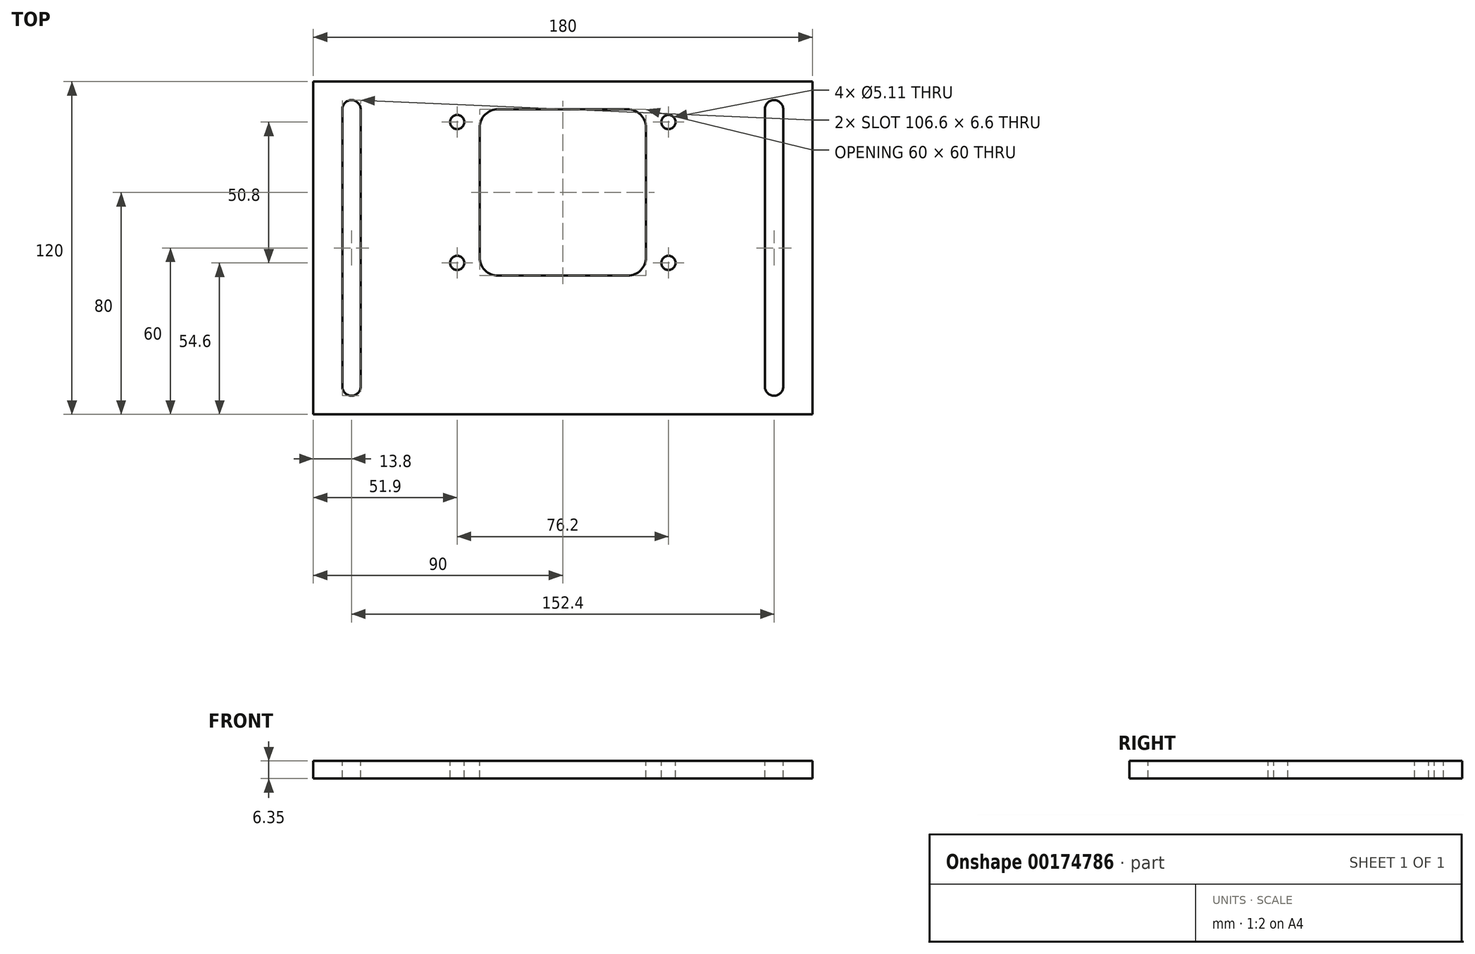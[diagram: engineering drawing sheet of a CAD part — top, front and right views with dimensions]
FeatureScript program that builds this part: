
annotation { "Feature Type Name" : "Feature", "Feature Type Description" : "" }
export const myFeature = defineFeature(function(context is Context, id is Id, definition is map)
    precondition{}
    {
        {
            var Q0;
            Q0=qCreatedBy(makeId("Top.planeOp"),FACE);
            var sketch = newSketch(context, id + "F0", { "sketchPlane" : qUnion([Q0])});
            skLineSegment(sketch, "E0.bottom", {"start": v(0, 0) * mm, "end": v(180, 0) * mm});
            skLineSegment(sketch, "E0.top", {"start": v(0, 120) * mm, "end": v(180, 120) * mm});
            skLineSegment(sketch, "E0.left", {"start": v(0, 0) * mm, "end": v(0, 120) * mm});
            skLineSegment(sketch, "E0.right", {"start": v(180, 0) * mm, "end": v(180, 120) * mm});
            skSolve(sketch);
        }
        {
            var Q0;
            Q0 = qSketchRegion(id + "F0", true);
            extrude(context, id + "F1", {"entities" : qUnion([Q0]), "depth" : 6.35 * mm});
        }
        {
            var Q0;
            Q0=makeQuery(id+"F1.opExtrude","CAP_FACE",FACE,{"disambiguationData":[OSD([sQuery(id+"F0.wireOp",EDGE,"E0.bottom"),sQuery(id+"F0.wireOp",EDGE,"E0.top"),sQuery(id+"F0.wireOp",EDGE,"E0.left"),sQuery(id+"F0.wireOp",EDGE,"E0.right")])],"isStart":false});
            var sketch = newSketch(context, id + "F2", { "sketchPlane" : qUnion([Q0])});
            skLineSegment(sketch, "E1", {"start": v(13.8, 110) * mm, "end": v(13.8, 10) * mm});
            skLineSegment(sketch, "E2", {"start": v(90, 120) * mm, "end": v(90, 0) * mm});
            skLineSegment(sketch, "E3", {"start": v(0, 60) * mm, "end": v(180, 60) * mm});
            skLineSegment(sketch, "E4.MirrorCS", {"start": v(166.2, 110) * mm, "end": v(166.2, 10) * mm});
            skArc(sketch, "E5.0.startCap", {"start": v(162.9, 110) * mm, "mid": v(166.2, 113.3) * mm, "end": v(169.5, 110) * mm});
            skArc(sketch, "E5.0.endCap", {"start": v(169.5, 10) * mm, "mid": v(166.2, 6.7) * mm, "end": v(162.9, 10) * mm});
            skLineSegment(sketch, "E5.0.left", {"start": v(169.5, 110) * mm, "end": v(169.5, 10) * mm});
            skLineSegment(sketch, "E5.0.right", {"start": v(162.9, 110) * mm, "end": v(162.9, 10) * mm});
            skArc(sketch, "E5.1.startCap", {"start": v(10.5, 110) * mm, "mid": v(13.8, 113.3) * mm, "end": v(17.1, 110) * mm});
            skArc(sketch, "E5.1.endCap", {"start": v(17.1, 10) * mm, "mid": v(13.8, 6.7) * mm, "end": v(10.5, 10) * mm});
            skLineSegment(sketch, "E5.1.left", {"start": v(17.1, 110) * mm, "end": v(17.1, 10) * mm});
            skLineSegment(sketch, "E5.1.right", {"start": v(10.5, 110) * mm, "end": v(10.5, 10) * mm});
            skSolve(sketch);
        }
        {
            var Q0;
            Q0 = qSketchRegion(id + "F2", true);
            extrude(context, id + "F3", {"entities" : qUnion([Q0]), "operationType" : NewBodyOperationType.REMOVE, "endBound" : BoundingType.THROUGH_ALL, "oppositeDirection" : true, "depth" : 25 * mm});
        }
        {
            var Q0;
            Q0=makeQuery(id+"F1.opExtrude","CAP_FACE",FACE,{"disambiguationData":[OSD([sQuery(id+"F0.wireOp",EDGE,"E0.bottom"),sQuery(id+"F0.wireOp",EDGE,"E0.top"),sQuery(id+"F0.wireOp",EDGE,"E0.left"),sQuery(id+"F0.wireOp",EDGE,"E0.right")])],"isStart":false});
            var sketch = newSketch(context, id + "F4", { "sketchPlane" : qUnion([Q0])});
            skLineSegment(sketch, "E6", {"start": v(90, 120) * mm, "end": v(90, 0) * mm});
            skLineSegment(sketch, "E7", {"start": v(0, 80) * mm, "end": v(180, 80) * mm});
            skLineSegment(sketch, "E8.bottom", {"start": v(113.4, 110) * mm, "end": v(66.6, 110) * mm});
            skLineSegment(sketch, "E8.top", {"start": v(113.4, 50) * mm, "end": v(66.6, 50) * mm});
            skLineSegment(sketch, "E8.left", {"start": v(120, 103.4) * mm, "end": v(120, 56.6) * mm});
            skLineSegment(sketch, "E8.right", {"start": v(60, 103.4) * mm, "end": v(60, 56.6) * mm});
            skPoint(sketch, "E8.middle", {"position": v(90, 80) * mm});
            skPoint(sketch, "E9.visualSharp", {"position": v(60, 110) * mm});
            skArc(sketch, "E9.filletArc", {"start": v(66.6, 110) * mm, "mid": v(61.93, 108.07) * mm, "end": v(60, 103.4) * mm});
            skPoint(sketch, "E10.visualSharp", {"position": v(120, 110) * mm});
            skArc(sketch, "E10.filletArc", {"start": v(120, 103.4) * mm, "mid": v(118.07, 108.07) * mm, "end": v(113.4, 110) * mm});
            skPoint(sketch, "E11.visualSharp", {"position": v(120, 50) * mm});
            skArc(sketch, "E11.filletArc", {"start": v(113.4, 50) * mm, "mid": v(118.07, 51.93) * mm, "end": v(120, 56.6) * mm});
            skPoint(sketch, "E12.visualSharp", {"position": v(60, 50) * mm});
            skArc(sketch, "E12.filletArc", {"start": v(60, 56.6) * mm, "mid": v(61.93, 51.93) * mm, "end": v(66.6, 50) * mm});
            skLineSegment(sketch, "E13", {"start": v(0, 60) * mm, "end": v(180, 60) * mm});
            skSolve(sketch);
        }
        {
            var Q0;
            Q0 = qSketchRegion(id + "F4", true);
            extrude(context, id + "F5", {"entities" : qUnion([Q0]), "operationType" : NewBodyOperationType.REMOVE, "endBound" : BoundingType.THROUGH_ALL, "oppositeDirection" : true, "depth" : 25 * mm});
        }
        {
            var Q0;
            Q0=makeQuery(id+"F1.opExtrude","CAP_FACE",FACE,{"disambiguationData":[OSD([sQuery(id+"F0.wireOp",EDGE,"E0.bottom"),sQuery(id+"F0.wireOp",EDGE,"E0.top"),sQuery(id+"F0.wireOp",EDGE,"E0.left"),sQuery(id+"F0.wireOp",EDGE,"E0.right")])],"isStart":false});
            var sketch = newSketch(context, id + "F6", { "sketchPlane" : qUnion([Q0])});
            skLineSegment(sketch, "E14", {"start": v(90, 120) * mm, "end": v(90, 0) * mm});
            skLineSegment(sketch, "E15", {"start": v(0, 80) * mm, "end": v(180, 80) * mm});
            skLineSegment(sketch, "E16.bottom", {"start": v(128.1, 54.6) * mm, "end": v(51.9, 54.6) * mm});
            skLineSegment(sketch, "E16.top", {"start": v(128.1, 105.4) * mm, "end": v(51.9, 105.4) * mm});
            skLineSegment(sketch, "E16.left", {"start": v(128.1, 54.6) * mm, "end": v(128.1, 105.4) * mm});
            skLineSegment(sketch, "E16.right", {"start": v(51.9, 54.6) * mm, "end": v(51.9, 105.4) * mm});
            skPoint(sketch, "E16.middle", {"position": v(90, 80) * mm});
            skLineSegment(sketch, "E17", {"start": v(0, 60) * mm, "end": v(180, 60) * mm});
            skSolve(sketch);
        }
        {
            var Q0;
            Q0=sQuery(id+"F6.wireOp",VERTEX,"E16.top.end");
            var Q1;
            Q1=sQuery(id+"F6.wireOp",VERTEX,"E16.top.start");
            var Q2;
            Q2=sQuery(id+"F6.wireOp",VERTEX,"E16.bottom.start");
            var Q3;
            Q3=sQuery(id+"F6.wireOp",VERTEX,"E16.bottom.end");
            var Q4;
            Q4=makeQuery(id+"F1.opExtrude","SWEPT_BODY",BODY,{"disambiguationData":[OSD([sQuery(id+"F0.wireOp",EDGE,"E0.bottom"),sQuery(id+"F0.wireOp",EDGE,"E0.top"),sQuery(id+"F0.wireOp",EDGE,"E0.left"),sQuery(id+"F0.wireOp",EDGE,"E0.right")])]});
            hole(context, id + "F7", {"style" : HoleStyle.SIMPLE, "endStyle" : HoleEndStyle.THROUGH, "standardTappedOrClearance" : lookupTablePath({ "standard" : "ANSI", "engagement" : "75%", "pitch" : "20 tpi", "size" : "1/4", "type" : "Tapped" }), "standardBlindInLast" : lookupTablePath({ "standard" : "ANSI", "engagement" : "75%", "pitch" : "20 tpi", "size" : "1/4", "type" : "Tapped" }), "holeDiameter" : 5.1 * mm, "locations" : qUnion([Q0, Q1, Q2, Q3]), "scope" : qUnion([Q4]), "isTappedThrough" : true, "majorDiameter" : 6.35 * mm, "showTappedDepth" : true});
        }
    });
